# Revit family: Sink-Undermount-Lavatory-KOHLER-Verticly-K-8192_1
name_source: partatom
category: Plumbing Fixtures
units: mm (PartAtom-declared; Revit-internal decimal feet)

## family parameters
Cut with Voids When Loaded = No
Host = Face
OmniClass Number = 23.31.13.00
OmniClass Title = Sinks
Part Type = Normal
Room Calculation Point = No
Round Connector Dimension = Use Diameter
Shared = No

## types (6) — shared parameters
ADA Compliant = No
Assembly Code = D2010400
CW Connection = No
Cold Water Inlet = Cold Water Inlet
Date Modified = 12/26/2023
Default Elevation = 36"
Description = Verticyl Trough Undercounter Lavatory
Drain Included = No
Flow Rate = 0 GPM
HW Connection = No
Height = 7 5/16"
Hot Water Inlet = Hot Water Inlet
Length = 42 7/16"
Manufacturer = Kohler Co.
Master Format 2014 = 22 41 16
Master Format 2014 Name = Residential Lavatories and Sinks
Material = Vitreous China
Pressure = 0.00 psi
Product Documentation Link = https://www.us.kohler.com
Product Name = Verticyl
Product Page URL = http://www.us.kohler.com
URL = https://www.us.kohler.com
Vent Connection = No
Waste Connection = Yes
Waste Water Outlet = Waste Water Outlet
WaterSense Certified = No
Width = 15 1/16"

## per-type parameters (varying)
| type | Finish | Model | Type |
| 0-White | Kohler-Vitreous_China-0-White | K-8192-0 | 1 |
| 96-Biscuit | Kohler-Vitreous_China-96-Biscuit | K-8192-96 | 5 |
| NY-Dune | Kohler-Vitreous_China-NY-Dune | K-8192-NY | 6 |
| 95-Ice Grey | Kohler-Vitreous_China-95-Ice_Grey | K-8192-95 | 4 |
| 58-Thunder Grey | Kohler-Vitreous_China-58-Thunder_Grey | K-8192-58 | 2 |
| 7-Black Black | Kohler-Vitreous_China-7-Black_Black | K-8192-7 | 3 |

## geometry (parser evidence)
native form markers: Sweep x4
no freeform markers — native parametric forms only
